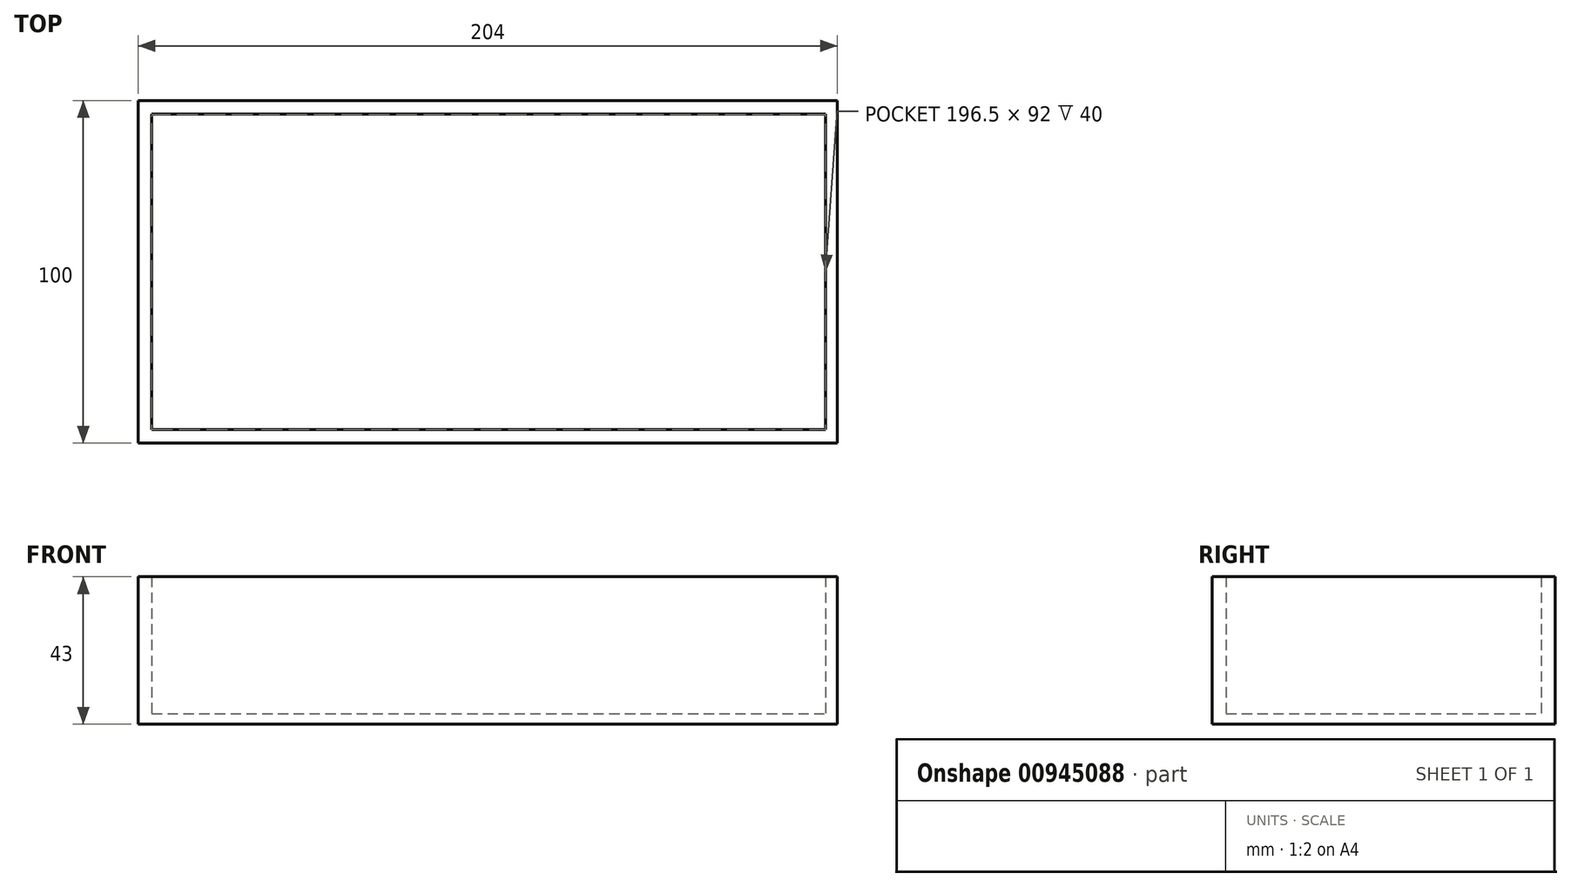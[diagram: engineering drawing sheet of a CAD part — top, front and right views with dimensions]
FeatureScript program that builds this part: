
annotation { "Feature Type Name" : "Feature", "Feature Type Description" : "" }
export const myFeature = defineFeature(function(context is Context, id is Id, definition is map)
    precondition{}
    {
        {
            var Q0;
            Q0=qCreatedBy(makeId("Top.planeOp"),FACE);
            var sketch = newSketch(context, id + "F0", { "sketchPlane" : qUnion([Q0])});
            skLineSegment(sketch, "E0.bottom", {"start": v(-102.5, 117.5) * mm, "end": v(102.5, 117.5) * mm, "construction": true});
            skLineSegment(sketch, "E0.top", {"start": v(-102.5, -117.5) * mm, "end": v(102.5, -117.5) * mm, "construction": true});
            skLineSegment(sketch, "E0.left", {"start": v(-102.5, 117.5) * mm, "end": v(-102.5, -117.5) * mm, "construction": true});
            skLineSegment(sketch, "E0.right", {"start": v(102.5, 117.5) * mm, "end": v(102.5, -117.5) * mm, "construction": true});
            skPoint(sketch, "E0.middle", {"position": v(0, 0) * mm});
            skSolve(sketch);
        }
        {
            var Q0;
            Q0=qCreatedBy(makeId("Top.planeOp"),FACE);
            var sketch = newSketch(context, id + "F1", { "sketchPlane" : qUnion([Q0])});
            skLineSegment(sketch, "E1.bottom", {"start": v(-102, -117) * mm, "end": v(102, -117) * mm});
            skLineSegment(sketch, "E1.top", {"start": v(-102, -17) * mm, "end": v(102, -17) * mm});
            skLineSegment(sketch, "E1.left", {"start": v(-102, -117) * mm, "end": v(-102, -17) * mm});
            skLineSegment(sketch, "E1.right", {"start": v(102, -117) * mm, "end": v(102, -17) * mm});
            skSolve(sketch);
        }
        {
            var Q0;
            Q0 = qSketchRegion(id + "F1", true);
            extrude(context, id + "F2", {"entities" : qUnion([Q0]), "depth" : 3 * mm, "offsetDistance" : 25 * mm});
        }
        {
            var Q0;
            Q0=makeQuery(id+"F2.opExtrude","CAP_FACE",FACE,{"disambiguationData":[OSD([sQuery(id+"F1.wireOp",EDGE,"E1.bottom"),sQuery(id+"F1.wireOp",EDGE,"E1.top"),sQuery(id+"F1.wireOp",EDGE,"E1.left"),sQuery(id+"F1.wireOp",EDGE,"E1.right")])],"isStart":false});
            var sketch = newSketch(context, id + "F3", { "sketchPlane" : qUnion([Q0])});
            skLineSegment(sketch, "E2.0.0", {"start": v(102, -17) * mm, "end": v(-102, -17) * mm});
            skLineSegment(sketch, "E2.0.1", {"start": v(-102, -17) * mm, "end": v(-102, -117) * mm});
            skLineSegment(sketch, "E2.0.2", {"start": v(-102, -117) * mm, "end": v(102, -117) * mm});
            skLineSegment(sketch, "E2.0.3", {"start": v(102, -117) * mm, "end": v(102, -17) * mm});
            skLineSegment(sketch, "E3.bottom", {"start": v(-98, -113) * mm, "end": v(98.5, -113) * mm});
            skLineSegment(sketch, "E3.top", {"start": v(-98, -21) * mm, "end": v(98.5, -21) * mm});
            skLineSegment(sketch, "E3.left", {"start": v(-98, -113) * mm, "end": v(-98, -21) * mm});
            skLineSegment(sketch, "E3.right", {"start": v(98.5, -113) * mm, "end": v(98.5, -21) * mm});
            skSolve(sketch);
        }
        {
            var Q0;
            Q0 = qSketchRegion(id + "F3", true);
            extrude(context, id + "F4", {"entities" : qUnion([Q0]), "operationType" : NewBodyOperationType.ADD, "depth" : 40 * mm, "offsetDistance" : 25 * mm});
        }
    });
